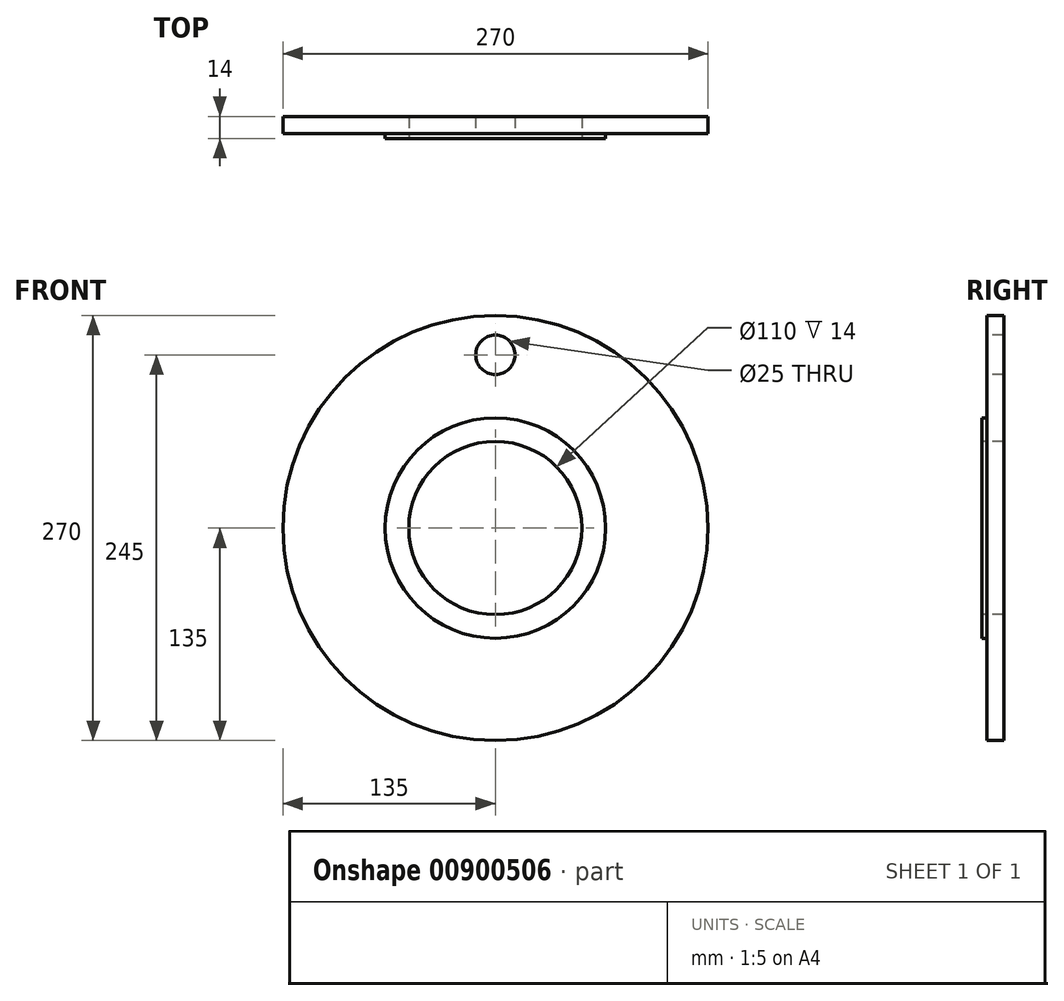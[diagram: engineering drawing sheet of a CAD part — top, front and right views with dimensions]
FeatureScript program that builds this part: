
annotation { "Feature Type Name" : "Feature", "Feature Type Description" : "" }
export const myFeature = defineFeature(function(context is Context, id is Id, definition is map)
    precondition{}
    {
        {
            var Q0;
            Q0=qCreatedBy(makeId("Right.planeOp"),FACE);
            var sketch = newSketch(context, id + "F0", { "sketchPlane" : qUnion([Q0])});
            skLineSegment(sketch, "E0", {"start": v(0, 55) * mm, "end": v(0, 70) * mm});
            skLineSegment(sketch, "E1", {"start": v(0, 70) * mm, "end": v(3, 70) * mm});
            skLineSegment(sketch, "E2", {"start": v(3, 70) * mm, "end": v(3, 135) * mm});
            skLineSegment(sketch, "E3", {"start": v(3, 135) * mm, "end": v(14, 135) * mm});
            skLineSegment(sketch, "E4", {"start": v(14, 135) * mm, "end": v(14, 55) * mm});
            skLineSegment(sketch, "E5", {"start": v(14, 55) * mm, "end": v(0, 55) * mm});
            skLineSegment(sketch, "E6", {"start": v(-67.05, 0) * mm, "end": v(130.71, 0) * mm, "construction": true});
            skSolve(sketch);
        }
        {
            var Q0;
            Q0=makeQuery(id+"F0.imprint","IMPRINT",FACE,{"disambiguationData":[TD([[makeQuery(id+"F0.imprint","IMPRINT",EDGE,{"derivedFrom":sQuery(id+"F0.wireOp",EDGE,"E0")}),-1.0]])]});
            var Q1;
            Q1=sQuery(id+"F0.wireOp",EDGE,"E6");
            revolve(context, id + "F1", {"surfaceOperationType" : NewSurfaceOperationType.NEW, "entities" : qUnion([Q0]), "axis" : qUnion([Q1]), "revolveType" : RevolveType.FULL});
        }
        {
            var Q0;
            Q0=makeQuery(id+"F1.opRevolve","SWEPT_FACE",FACE,{"disambiguationData":[OSD([sQuery(id+"F0.wireOp",EDGE,"E2")])]});
            var sketch = newSketch(context, id + "F2", { "sketchPlane" : qUnion([Q0])});
            skPoint(sketch, "E7", {"position": v(0, 110) * mm});
            skPoint(sketch, "E8.center", {"position": v(0, 0) * mm});
            skSolve(sketch);
        }
        {
            var Q0;
            Q0=sQuery(id+"F2.wireOp",VERTEX,"E7");
            var Q1;
            Q1=makeQuery(id+"F1.opRevolve","SWEPT_BODY",BODY,{"disambiguationData":[OSD([sQuery(id+"F0.wireOp",EDGE,"E0"),sQuery(id+"F0.wireOp",EDGE,"E1"),sQuery(id+"F0.wireOp",EDGE,"E2"),sQuery(id+"F0.wireOp",EDGE,"E3"),sQuery(id+"F0.wireOp",EDGE,"E4"),sQuery(id+"F0.wireOp",EDGE,"E5")])]});
            hole(context, id + "F3", {"style" : HoleStyle.SIMPLE, "endStyle" : HoleEndStyle.THROUGH, "holeDiameter" : 25 * mm, "majorDiameter" : 5 * mm, "isTappedThrough" : true, "tappedDepth" : 12 * mm, "tapClearance" : 3, "locations" : qUnion([Q0]), "scope" : qUnion([Q1])});
        }
    });
